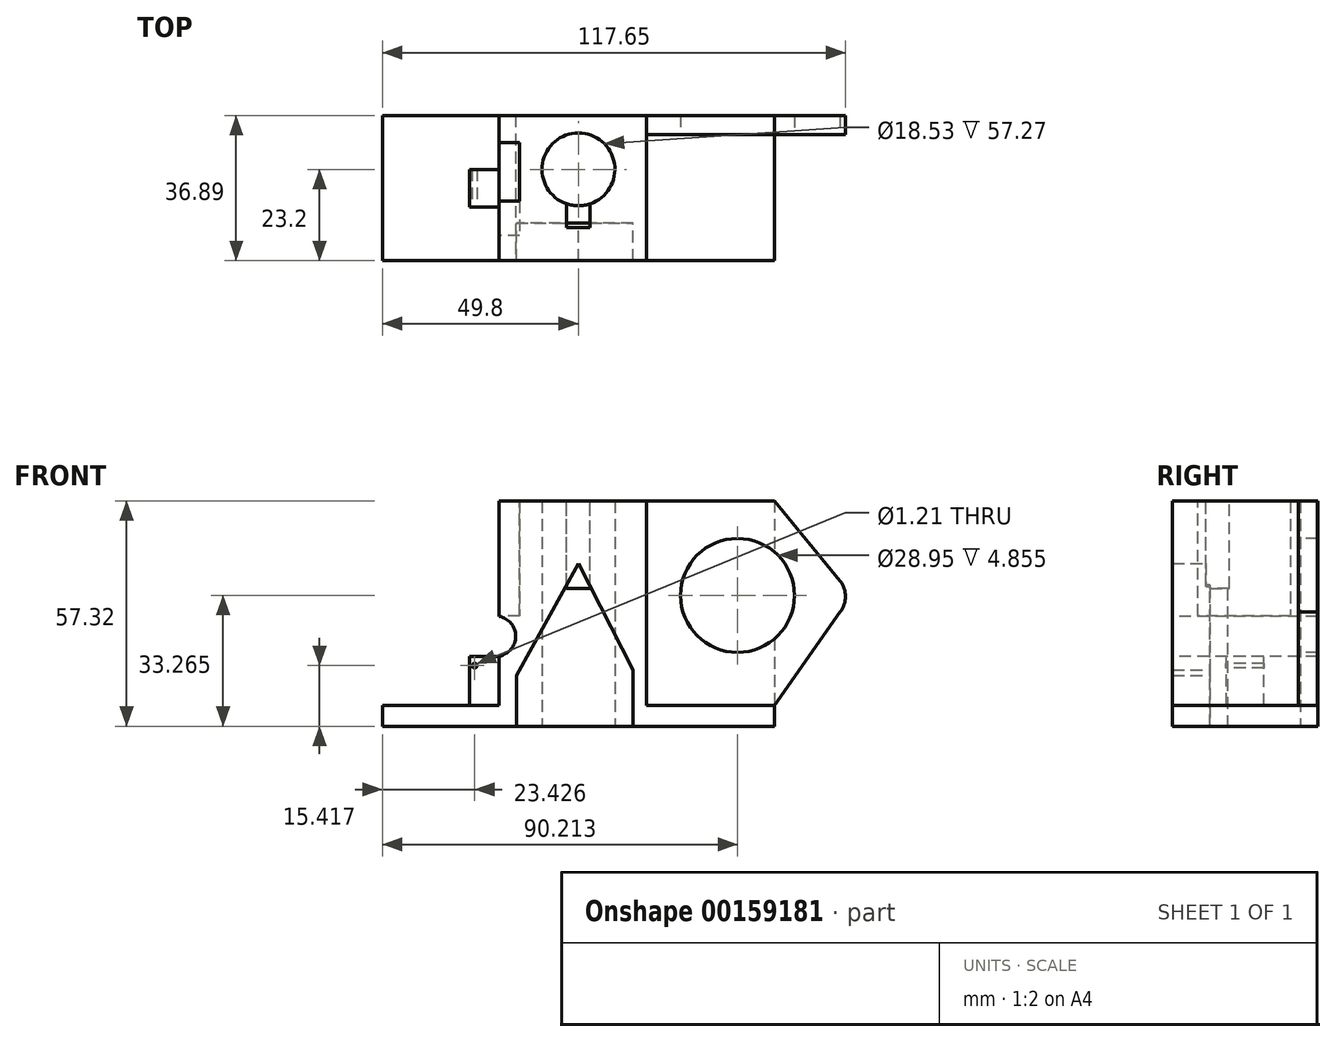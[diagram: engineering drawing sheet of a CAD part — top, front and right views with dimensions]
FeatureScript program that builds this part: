
annotation { "Feature Type Name" : "Feature", "Feature Type Description" : "" }
export const myFeature = defineFeature(function(context is Context, id is Id, definition is map)
    precondition{}
    {
        {
            var Q0;
            Q0=qCreatedBy(makeId("Top.planeOp"),FACE);
            var sketch = newSketch(context, id + "F0", { "sketchPlane" : qUnion([Q0])});
            skLineSegment(sketch, "E0.bottom", {"start": v(49.8, 13.69) * mm, "end": v(-49.8, 13.69) * mm});
            skLineSegment(sketch, "E0.top", {"start": v(49.8, -13.69) * mm, "end": v(-49.8, -13.69) * mm});
            skLineSegment(sketch, "E0.left", {"start": v(49.8, 13.69) * mm, "end": v(49.8, -13.69) * mm});
            skLineSegment(sketch, "E0.right", {"start": v(-49.8, 13.69) * mm, "end": v(-49.8, -13.69) * mm});
            skPoint(sketch, "E0.middle", {"position": v(0, 0) * mm});
            skCircle(sketch, "E1", {"center": v(0, 0) * mm, "radius": 9.27 * mm});
            skPoint(sketch, "E2", {"position": v(-14.12, 13.69) * mm});
            skPoint(sketch, "E3", {"position": v(-14.12, -13.69) * mm});
            skPoint(sketch, "E4", {"position": v(12.53, -13.69) * mm});
            skPoint(sketch, "E5", {"position": v(12.53, 13.69) * mm});
            skSolve(sketch);
        }
        {
            var Q0;
            Q0=makeQuery(id+"F0.imprint","IMPRINT",FACE,{"disambiguationData":[TD([[makeQuery(id+"F0.imprint","IMPRINT",EDGE,{"derivedFrom":sQuery(id+"F0.wireOp",EDGE,"E0.bottom")}),1.0]])]});
            extrude(context, id + "F1", {"entities" : qUnion([Q0]), "depth" : 5.32 * mm});
        }
        {
            var Q0;
            Q0=makeQuery(id+"F1.opExtrude","CAP_FACE",FACE,{"disambiguationData":[OSD([sQuery(id+"F0.wireOp",EDGE,"E0.bottom"),sQuery(id+"F0.wireOp",EDGE,"E0.top"),sQuery(id+"F0.wireOp",EDGE,"E0.left"),sQuery(id+"F0.wireOp",EDGE,"E0.right"),sQuery(id+"F0.wireOp",EDGE,"E1")])],"isStart":false});
            var sketch = newSketch(context, id + "F2", { "sketchPlane" : qUnion([Q0])});
            skLineSegment(sketch, "E6", {"start": v(-20.16, 13.69) * mm, "end": v(-20.16, -13.69) * mm});
            skLineSegment(sketch, "E7", {"start": v(17.24, 13.69) * mm, "end": v(17.24, -13.69) * mm});
            skLineSegment(sketch, "E8", {"start": v(-20.16, -13.69) * mm, "end": v(17.24, -13.69) * mm});
            skLineSegment(sketch, "E9", {"start": v(-20.16, 13.69) * mm, "end": v(17.24, 13.69) * mm});
            skSolve(sketch);
        }
        {
            var Q0;
            {var subQ0=sQuery(id+"F2.wireOp",EDGE,"E6");Q0=makeQuery(id+"F2.imprint","IMPRINT",FACE,{"disambiguationData":[TD([[makeQuery(id+"F2.imprint","IMPRINT",EDGE,{"derivedFrom":subQ0}),1.0]])]});}
            extrude(context, id + "F3", {"entities" : qUnion([Q0]), "operationType" : NewBodyOperationType.ADD, "depth" : 51.95 * mm});
        }
        {
            var Q0;
            Q0=makeQuery(id+"F3.boolean.opBoolean","MERGE",FACE,{"derivedFrom":[makeQuery(id+"F1.opExtrude","SWEPT_FACE",FACE,{"disambiguationData":[OSD([sQuery(id+"F0.wireOp",EDGE,"E0.top")])]}),makeQuery(id+"F3.opExtrude","SWEPT_FACE",FACE,{"disambiguationData":[OSD([sQuery(id+"F2.wireOp",EDGE,"E8")])]})]});
            var sketch = newSketch(context, id + "F4", { "sketchPlane" : qUnion([Q0])});
            skLineSegment(sketch, "E10", {"start": v(-15.78, 0) * mm, "end": v(-15.78, 12.9) * mm});
            skLineSegment(sketch, "E11", {"start": v(-15.78, 12.9) * mm, "end": v(0, 41.43) * mm});
            skLineSegment(sketch, "E12", {"start": v(0, 41.43) * mm, "end": v(13.87, 14.3) * mm});
            skLineSegment(sketch, "E13", {"start": v(13.87, 14.3) * mm, "end": v(13.87, 0) * mm});
            skSolve(sketch);
        }
        {
            var Q0;
            {var subQ10=sQuery(id+"F4.wireOp",EDGE,"E10");Q0=makeQuery(id+"F4.imprint","IMPRINT",FACE,{"disambiguationData":[TD([[makeQuery(id+"F4.imprint","IMPRINT",EDGE,{"derivedFrom":subQ10}),1.0]])]});}
            extrude(context, id + "F5", {"entities" : qUnion([Q0]), "operationType" : NewBodyOperationType.ADD, "depth" : 9.52 * mm});
        }
        {
            var Q0;
            {var subQ0=sQuery(id+"F2.wireOp",EDGE,"E8");Q0=makeQuery(id+"F5.boolean.opBoolean","MERGE",FACE,{"derivedFrom":[makeQuery(id+"F3.opExtrude","CAP_FACE",FACE,{"disambiguationData":[OSD([sQuery(id+"F0.wireOp",EDGE,"E1"),sQuery(id+"F2.wireOp",EDGE,"E6"),sQuery(id+"F2.wireOp",EDGE,"E7"),subQ0,sQuery(id+"F2.wireOp",EDGE,"E9")])],"isStart":false}),makeQuery(id+"F5.opExtrude","SWEPT_FACE",FACE,{"disambiguationData":[OSD([subQ0])]})]});}
            var sketch = newSketch(context, id + "F6", { "sketchPlane" : qUnion([Q0])});
            skLineSegment(sketch, "E14", {"start": v(-3.04, -8.75) * mm, "end": v(-3.04, -14.75) * mm});
            skLineSegment(sketch, "E15", {"start": v(-3.04, -14.75) * mm, "end": v(3, -14.75) * mm});
            skLineSegment(sketch, "E16", {"start": v(3, -14.75) * mm, "end": v(3, -8.76) * mm});
            skSolve(sketch);
        }
        {
            var Q0;
            {var subQ0=sQuery(id+"F6.wireOp",EDGE,"E14");Q0=makeQuery(id+"F6.imprint","IMPRINT",FACE,{"disambiguationData":[TD([[makeQuery(id+"F6.imprint","IMPRINT",EDGE,{"derivedFrom":subQ0}),1.0]])]});}
            extrude(context, id + "F7", {"entities" : qUnion([Q0]), "operationType" : NewBodyOperationType.REMOVE, "oppositeDirection" : true, "depth" : 22.25 * mm});
        }
        {
            var Q0;
            {var subQ0=sQuery(id+"F2.wireOp",EDGE,"E6");Q0=makeQuery(id+"F5.boolean.opBoolean","MERGE",FACE,{"derivedFrom":[makeQuery(id+"F3.opExtrude","SWEPT_FACE",FACE,{"disambiguationData":[OSD([subQ0])]}),makeQuery(id+"F5.opExtrude","SWEPT_FACE",FACE,{"disambiguationData":[OSD([sQuery(id+"F0.wireOp",EDGE,"E0.top"),subQ0,sQuery(id+"F2.wireOp",EDGE,"E8")])]})]});}
            var sketch = newSketch(context, id + "F8", { "sketchPlane" : qUnion([Q0])});
            skLineSegment(sketch, "E17", {"start": v(-13.69, 27.8) * mm, "end": v(23.2, 27.8) * mm});
            skLineSegment(sketch, "E18", {"start": v(-13.69, 17.98) * mm, "end": v(23.2, 17.98) * mm});
            skSolve(sketch);
        }
        {
            var Q0;
            Q0=makeQuery(id+"F5.opExtrude","CAP_FACE",FACE,{"disambiguationData":[OSD([sQuery(id+"F0.wireOp",EDGE,"E0.top"),sQuery(id+"F0.wireOp",EDGE,"E0.left"),sQuery(id+"F0.wireOp",EDGE,"E0.right"),sQuery(id+"F2.wireOp",EDGE,"E6"),sQuery(id+"F2.wireOp",EDGE,"E7"),sQuery(id+"F2.wireOp",EDGE,"E8"),sQuery(id+"F4.wireOp",EDGE,"E10"),sQuery(id+"F4.wireOp",EDGE,"E11"),sQuery(id+"F4.wireOp",EDGE,"E12"),sQuery(id+"F4.wireOp",EDGE,"E13")])],"isStart":false});
            var sketch = newSketch(context, id + "F9", { "sketchPlane" : qUnion([Q0])});
            skArc(sketch, "E19", {"start": v(-20.16, 17.82) * mm, "mid": v(-15.96, 22.9) * mm, "end": v(-20.16, 27.97) * mm});
            skSolve(sketch);
        }
        {
            var Q0;
            Q0 = qSketchRegion(id + "F9", true);
            var Q1;
            {var subQ0=sQuery(id+"F9.wireOp",EDGE,"E19");Q1=makeQuery(id+"F9.imprint","IMPRINT",FACE,{"disambiguationData":[TD([[makeQuery(id+"F9.imprint","IMPRINT",EDGE,{"derivedFrom":subQ0}),1.0]])]});}
            extrude(context, id + "F10", {"entities" : qUnion([Q0, Q1]), "operationType" : NewBodyOperationType.REMOVE, "oppositeDirection" : true, "depth" : 37.48 * mm});
        }
        {
            var Q0;
            {var subQ0=sQuery(id+"F8.wireOp",EDGE,"E18");Q0=makeQuery(id+"F8.imprint","IMPRINT",FACE,{"disambiguationData":[TD([[makeQuery(id+"F8.imprint","IMPRINT",EDGE,{"derivedFrom":subQ0}),-1.0]])]});}
            var sketch = newSketch(context, id + "F11", { "sketchPlane" : qUnion([Q0])});
            skLineSegment(sketch, "E20", {"start": v(0, 5.42) * mm, "end": v(0, 17.74) * mm});
            skLineSegment(sketch, "E21", {"start": v(0, 17.74) * mm, "end": v(9.6, 17.74) * mm});
            skLineSegment(sketch, "E22", {"start": v(9.6, 17.74) * mm, "end": v(9.6, 5.34) * mm});
            skLineSegment(sketch, "E23", {"start": v(9.6, 5.34) * mm, "end": v(0, 5.42) * mm});
            skSolve(sketch);
        }
        {
            var Q0;
            Q0=makeQuery(id+"F11.imprint","IMPRINT",FACE,{"disambiguationData":[TD([[makeQuery(id+"F11.imprint","IMPRINT",EDGE,{"derivedFrom":sQuery(id+"F11.wireOp",EDGE,"E20")}),-1.0]])]});
            extrude(context, id + "F12", {"entities" : qUnion([Q0]), "operationType" : NewBodyOperationType.ADD, "depth" : 7.5 * mm});
        }
        {
            var Q0;
            {var subQ0=sQuery(id+"F8.wireOp",EDGE,"E17");Q0=makeQuery(id+"F8.imprint","IMPRINT",FACE,{"disambiguationData":[TD([[makeQuery(id+"F8.imprint","IMPRINT",EDGE,{"derivedFrom":subQ0}),1.0]])]});}
            var sketch = newSketch(context, id + "F13", { "sketchPlane" : qUnion([Q0])});
            skLineSegment(sketch, "E24", {"start": v(-6.77, 57.63) * mm, "end": v(-6.77, 28.07) * mm});
            skLineSegment(sketch, "E25", {"start": v(-6.77, 28.07) * mm, "end": v(16.81, 28.07) * mm});
            skLineSegment(sketch, "E26", {"start": v(16.81, 28.07) * mm, "end": v(16.81, 57.06) * mm});
            skLineSegment(sketch, "E27", {"start": v(16.81, 57.06) * mm, "end": v(-6.77, 57.63) * mm});
            skSolve(sketch);
        }
        {
            var Q0;
            {var subQ7=sQuery(id+"F13.wireOp",EDGE,"E25");Q0=makeQuery(id+"F13.imprint","IMPRINT",FACE,{"disambiguationData":[TD([[makeQuery(id+"F13.imprint","IMPRINT",EDGE,{"derivedFrom":subQ7}),1.0]])]});}
            extrude(context, id + "F14", {"entities" : qUnion([Q0]), "operationType" : NewBodyOperationType.REMOVE, "oppositeDirection" : true, "depth" : 5.25 * mm});
        }
        {
            var Q0;
            Q0=makeQuery(id+"F12.opExtrude","SWEPT_FACE",FACE,{"disambiguationData":[OSD([sQuery(id+"F11.wireOp",EDGE,"E22")])]});
            var sketch = newSketch(context, id + "F15", { "sketchPlane" : qUnion([Q0])});
            skCircle(sketch, "E28", {"center": v(-26.37, 15.42) * mm, "radius": 0.6 * mm});
            skSolve(sketch);
        }
        {
            var Q0;
            Q0=makeQuery(id+"F15.imprint","IMPRINT",FACE,{"disambiguationData":[TD([[makeQuery(id+"F15.imprint","IMPRINT",EDGE,{"derivedFrom":sQuery(id+"F15.wireOp",EDGE,"E28")}),1.0]])]});
            extrude(context, id + "F16", {"entities" : qUnion([Q0]), "operationType" : NewBodyOperationType.REMOVE, "oppositeDirection" : true, "depth" : 25 * mm});
        }
        {
            var Q0;
            Q0=makeQuery(id+"F12.opExtrude","SWEPT_FACE",FACE,{"disambiguationData":[OSD([sQuery(id+"F11.wireOp",EDGE,"E22")])]});
            var sketch = newSketch(context, id + "F17", { "sketchPlane" : qUnion([Q0])});
            skArc(sketch, "E29", {"start": v(-27.66, 5.34) * mm, "mid": v(-28.48, 9.78) * mm, "end": v(-30.83, 13.64) * mm});
            skArc(sketch, "E30", {"start": v(-31.54, 18.73) * mm, "mid": v(-32.13, 16.05) * mm, "end": v(-30.83, 13.64) * mm});
            skLineSegment(sketch, "E31", {"start": v(-31.54, 18.73) * mm, "end": v(-29.77, 18.73) * mm});
            skLineSegment(sketch, "E32", {"start": v(-29.77, 18.73) * mm, "end": v(-27.66, 17.74) * mm});
            skSolve(sketch);
        }
        {
            var Q0;
            {var subQ1=sQuery(id+"F0.wireOp",EDGE,"E0.left");var subQ2=makeQuery(id+"F1.opExtrude","SWEPT_FACE",FACE,{"disambiguationData":[OSD([subQ1])]});var subQ3=sQuery(id+"F0.wireOp",EDGE,"E0.top");var subQ5=sQuery(id+"F0.wireOp",EDGE,"E0.bottom");var subQ6=makeQuery(id+"F1.opExtrude","CAP_FACE",FACE,{"disambiguationData":[OSD([subQ5,subQ3,subQ1,sQuery(id+"F0.wireOp",EDGE,"E0.right"),sQuery(id+"F0.wireOp",EDGE,"E1")])],"isStart":false});Q0=makeQuery(id+"F5.boolean.opBoolean","MERGE",FACE,{"derivedFrom":[makeQuery(id+"F3.boolean.opBoolean","SPLIT",FACE,{"disambiguationData":[TD([subQ2])],"derivedFrom":subQ6}),makeQuery(id+"F5.opExtrude","SWEPT_FACE",FACE,{"disambiguationData":[OSD([subQ3]),TDD([makeQuery(id+"F4.imprint","IMPRINT",EDGE,{"derivedFrom":makeQuery(id+"F3.boolean.opBoolean","SPLIT",EDGE,{"disambiguationData":[TD([subQ2])],"derivedFrom":makeQuery(id+"F1.opExtrude","CAP_EDGE",EDGE,{"disambiguationData":[OSD([subQ3])],"isStart":false})})})])]})]});}
            var sketch = newSketch(context, id + "F18", { "sketchPlane" : qUnion([Q0])});
            skLineSegment(sketch, "E33", {"start": v(17.24, 8.83) * mm, "end": v(49.8, 8.83) * mm});
            skSolve(sketch);
        }
        {
            var Q0;
            {var subQ0=sQuery(id+"F18.wireOp",EDGE,"E33");Q0=makeQuery(id+"F18.imprint","IMPRINT",FACE,{"disambiguationData":[TD([[makeQuery(id+"F18.imprint","IMPRINT",EDGE,{"derivedFrom":subQ0}),1.0]])]});}
            extrude(context, id + "F19", {"entities" : qUnion([Q0]), "operationType" : NewBodyOperationType.ADD, "depth" : 52 * mm});
        }
        {
            var Q0;
            Q0=makeQuery(id+"F19.opExtrude","SWEPT_FACE",FACE,{"disambiguationData":[OSD([sQuery(id+"F18.wireOp",EDGE,"E33")])]});
            var sketch = newSketch(context, id + "F20", { "sketchPlane" : qUnion([Q0])});
            skLineSegment(sketch, "E34", {"start": v(17.24, 33.26) * mm, "end": v(49.8, 33.26) * mm});
            skLineSegment(sketch, "E35", {"start": v(49.8, 57.32) * mm, "end": v(66.44, 36.98) * mm});
            skArc(sketch, "E36", {"start": v(66.44, 29.03) * mm, "mid": v(67.85, 33) * mm, "end": v(66.44, 36.98) * mm});
            skLineSegment(sketch, "E37", {"start": v(66.44, 29.03) * mm, "end": v(49.8, 5.32) * mm});
            skCircle(sketch, "E38", {"center": v(40.41, 33.26) * mm, "radius": 14.47 * mm});
            skSolve(sketch);
        }
        {
            var Q0;
            {var subQ0=sQuery(id+"F20.wireOp",EDGE,"E35");Q0=makeQuery(id+"F20.imprint","IMPRINT",FACE,{"disambiguationData":[TD([[makeQuery(id+"F20.imprint","IMPRINT",EDGE,{"derivedFrom":subQ0}),-1.0]])]});}
            extrude(context, id + "F21", {"entities" : qUnion([Q0]), "operationType" : NewBodyOperationType.ADD, "oppositeDirection" : true, "depth" : 4.83 * mm});
        }
        {
            var Q0;
            Q0 = qSketchRegion(id + "F20", true);
            extrude(context, id + "F22", {"entities" : qUnion([Q0]), "operationType" : NewBodyOperationType.REMOVE, "oppositeDirection" : true, "depth" : 25 * mm});
        }
    });
